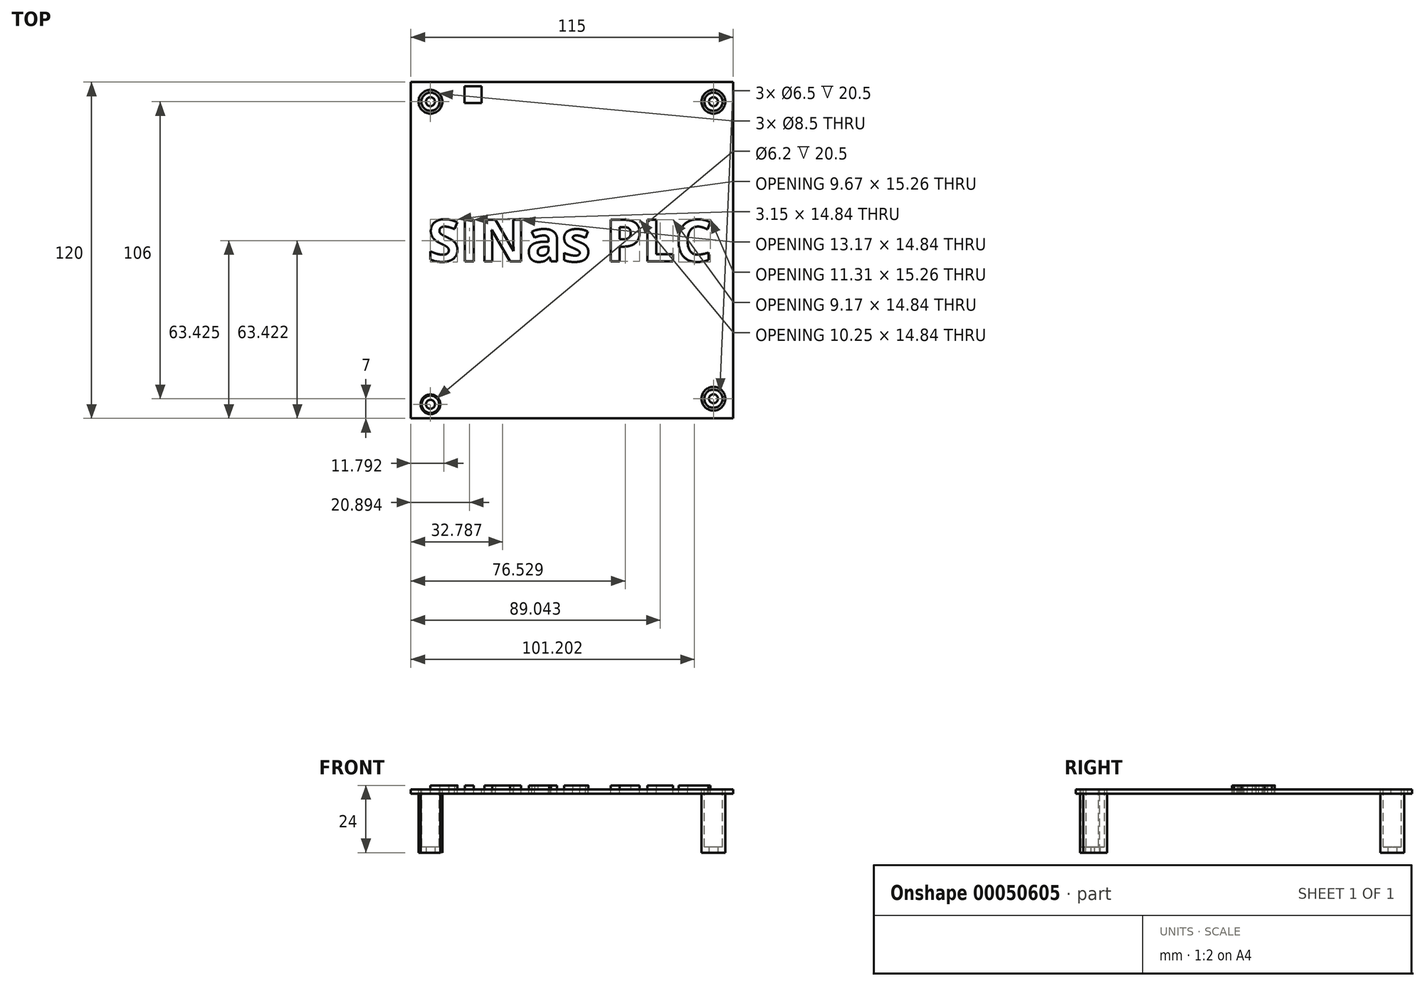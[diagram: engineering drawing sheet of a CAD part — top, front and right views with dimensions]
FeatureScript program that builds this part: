
annotation { "Feature Type Name" : "Feature", "Feature Type Description" : "" }
export const myFeature = defineFeature(function(context is Context, id is Id, definition is map)
    precondition{}
    {
        {
            var Q0;
            Q0=qCreatedBy(makeId("Top.planeOp"),FACE);
            var sketch = newSketch(context, id + "F0", { "sketchPlane" : qUnion([Q0])});
            skLineSegment(sketch, "E0.bottom", {"start": v(-52.5, 65) * mm, "end": v(62.5, 65) * mm});
            skLineSegment(sketch, "E0.top", {"start": v(-52.5, -55) * mm, "end": v(62.5, -55) * mm});
            skLineSegment(sketch, "E0.left", {"start": v(-52.5, 65) * mm, "end": v(-52.5, -55) * mm});
            skLineSegment(sketch, "E0.right", {"start": v(62.5, 65) * mm, "end": v(62.5, -55) * mm});
            skLineSegment(sketch, "E1.rect.bottom", {"start": v(-27.3, 57.5) * mm, "end": v(-33.3, 57.5) * mm});
            skLineSegment(sketch, "E1.rect.top", {"start": v(-27.3, 63.5) * mm, "end": v(-33.3, 63.5) * mm});
            skLineSegment(sketch, "E1.rect.left", {"start": v(-27.3, 57.5) * mm, "end": v(-27.3, 63.5) * mm});
            skLineSegment(sketch, "E1.rect.right", {"start": v(-33.3, 57.5) * mm, "end": v(-33.3, 63.5) * mm});
            skPoint(sketch, "E1.rect.middle", {"position": v(-30.3, 60.5) * mm});
            skCircle(sketch, "E2", {"center": v(-45.5, 58) * mm, "radius": 4.25 * mm});
            skCircle(sketch, "E3", {"center": v(55.5, 58) * mm, "radius": 4.25 * mm});
            skCircle(sketch, "E4", {"center": v(55.5, -48) * mm, "radius": 4.25 * mm});
            skCircle(sketch, "E5", {"center": v(-45.5, -50) * mm, "radius": 3.5 * mm});
            skText(sketch, "E6", { "text": "SINas PLC", "fontName": "OpenSans-Bold.ttf"});
            const initialGuessF0  = {"E6": [-0.0465, 0.001, 1, 0, 0.01497]};
            skSetInitialGuess(sketch, initialGuessF0);
            skSolve(sketch);
        }
        {
            var Q0;
            Q0=makeQuery(id+"F0.imprint","IMPRINT",FACE,{"disambiguationData":[TD([[makeQuery(id+"F0.imprint","IMPRINT",EDGE,{"derivedFrom":sQuery(id+"F0.wireOp",EDGE,"E0.bottom")}),-1.0]])]});
            extrude(context, id + "F1", {"entities" : qUnion([Q0]), "oppositeDirection" : true, "depth" : 1.5 * mm});
        }
        {
            var Q0;
            Q0=makeQuery(id+"F0.imprint","IMPRINT",FACE,{"disambiguationData":[TD([[makeQuery(id+"F0.imprint","IMPRINT",EDGE,{"derivedFrom":sQuery(id+"F0.wireOp",EDGE,"E2")}),1.0]])]});
            var Q1;
            Q1=makeQuery(id+"F0.imprint","IMPRINT",FACE,{"disambiguationData":[TD([[makeQuery(id+"F0.imprint","IMPRINT",EDGE,{"derivedFrom":sQuery(id+"F0.wireOp",EDGE,"E3")}),1.0]])]});
            var Q2;
            Q2=makeQuery(id+"F0.imprint","IMPRINT",FACE,{"disambiguationData":[TD([[makeQuery(id+"F0.imprint","IMPRINT",EDGE,{"derivedFrom":sQuery(id+"F0.wireOp",EDGE,"E5")}),1.0]])]});
            var Q3;
            Q3=makeQuery(id+"F0.imprint","IMPRINT",FACE,{"disambiguationData":[TD([[makeQuery(id+"F0.imprint","IMPRINT",EDGE,{"derivedFrom":sQuery(id+"F0.wireOp",EDGE,"E4")}),1.0]])]});
            extrude(context, id + "F2", {"entities" : qUnion([Q0, Q1, Q2, Q3]), "oppositeDirection" : true, "depth" : 22.5 * mm});
        }
        {
            var Q0;
            Q0=makeQuery(id+"F2.opExtrude","CAP_FACE",FACE,{"disambiguationData":[OSD([sQuery(id+"F0.wireOp",EDGE,"E3")])],"isStart":true});
            var sketch = newSketch(context, id + "F3", { "sketchPlane" : qUnion([Q0])});
            skCircle(sketch, "E7", {"center": v(55.5, 58) * mm, "radius": 3.25 * mm});
            skSolve(sketch);
        }
        {
            var Q0;
            Q0=makeQuery(id+"F3.imprint","IMPRINT",FACE,{"disambiguationData":[TD([[makeQuery(id+"F3.imprint","IMPRINT",EDGE,{"derivedFrom":sQuery(id+"F3.wireOp",EDGE,"E7")}),1.0]])]});
            extrude(context, id + "F4", {"entities" : qUnion([Q0]), "operationType" : NewBodyOperationType.REMOVE, "oppositeDirection" : true, "depth" : 20.5 * mm});
        }
        {
            var Q0;
            Q0=makeQuery(id+"F2.opExtrude","CAP_FACE",FACE,{"disambiguationData":[OSD([sQuery(id+"F0.wireOp",EDGE,"E2")])],"isStart":true});
            var sketch = newSketch(context, id + "F5", { "sketchPlane" : qUnion([Q0])});
            skCircle(sketch, "E8", {"center": v(-45.5, 58) * mm, "radius": 3.25 * mm});
            skSolve(sketch);
        }
        {
            var Q0;
            Q0=makeQuery(id+"F5.imprint","IMPRINT",FACE,{"disambiguationData":[TD([[makeQuery(id+"F5.imprint","IMPRINT",EDGE,{"derivedFrom":sQuery(id+"F5.wireOp",EDGE,"E8")}),1.0]])]});
            extrude(context, id + "F6", {"entities" : qUnion([Q0]), "operationType" : NewBodyOperationType.REMOVE, "oppositeDirection" : true, "depth" : 20.5 * mm});
        }
        {
            var Q0;
            Q0=makeQuery(id+"F2.opExtrude","CAP_FACE",FACE,{"disambiguationData":[OSD([sQuery(id+"F0.wireOp",EDGE,"E5")])],"isStart":true});
            var sketch = newSketch(context, id + "F7", { "sketchPlane" : qUnion([Q0])});
            skCircle(sketch, "E9", {"center": v(-45.5, -50) * mm, "radius": 3.1 * mm});
            skSolve(sketch);
        }
        {
            var Q0;
            Q0=makeQuery(id+"F7.imprint","IMPRINT",FACE,{"disambiguationData":[TD([[makeQuery(id+"F7.imprint","IMPRINT",EDGE,{"derivedFrom":sQuery(id+"F7.wireOp",EDGE,"E9")}),1.0]])]});
            extrude(context, id + "F8", {"entities" : qUnion([Q0]), "operationType" : NewBodyOperationType.REMOVE, "oppositeDirection" : true, "depth" : 20.5 * mm});
        }
        {
            var Q0;
            Q0=makeQuery(id+"F2.opExtrude","CAP_FACE",FACE,{"disambiguationData":[OSD([sQuery(id+"F0.wireOp",EDGE,"E4")])],"isStart":true});
            var sketch = newSketch(context, id + "F9", { "sketchPlane" : qUnion([Q0])});
            skCircle(sketch, "E10", {"center": v(55.5, -48) * mm, "radius": 3.25 * mm});
            skSolve(sketch);
        }
        {
            var Q0;
            Q0=makeQuery(id+"F9.imprint","IMPRINT",FACE,{"disambiguationData":[TD([[makeQuery(id+"F9.imprint","IMPRINT",EDGE,{"derivedFrom":sQuery(id+"F9.wireOp",EDGE,"E10")}),1.0]])]});
            extrude(context, id + "F10", {"entities" : qUnion([Q0]), "operationType" : NewBodyOperationType.REMOVE, "oppositeDirection" : true, "depth" : 20.5 * mm});
        }
        {
            var Q0;
            Q0=makeQuery(id+"F2.opExtrude","CAP_FACE",FACE,{"disambiguationData":[OSD([sQuery(id+"F0.wireOp",EDGE,"E5")])],"isStart":false});
            var sketch = newSketch(context, id + "F11", { "sketchPlane" : qUnion([Q0])});
            skCircle(sketch, "E11", {"center": v(-45.5, 50) * mm, "radius": 1.6 * mm});
            skSolve(sketch);
        }
        {
            var Q0;
            Q0=makeQuery(id+"F11.imprint","IMPRINT",FACE,{"disambiguationData":[TD([[makeQuery(id+"F11.imprint","IMPRINT",EDGE,{"derivedFrom":sQuery(id+"F11.wireOp",EDGE,"E11")}),1.0]])]});
            extrude(context, id + "F12", {"entities" : qUnion([Q0]), "operationType" : NewBodyOperationType.REMOVE, "oppositeDirection" : true, "depth" : 2.5 * mm});
        }
        {
            var Q0;
            Q0=makeQuery(id+"F2.opExtrude","CAP_FACE",FACE,{"disambiguationData":[OSD([sQuery(id+"F0.wireOp",EDGE,"E2")])],"isStart":false});
            var sketch = newSketch(context, id + "F13", { "sketchPlane" : qUnion([Q0])});
            skCircle(sketch, "E12", {"center": v(-45.5, -58) * mm, "radius": 1.6 * mm});
            skSolve(sketch);
        }
        {
            var Q0;
            Q0=makeQuery(id+"F13.imprint","IMPRINT",FACE,{"disambiguationData":[TD([[makeQuery(id+"F13.imprint","IMPRINT",EDGE,{"derivedFrom":sQuery(id+"F13.wireOp",EDGE,"E12")}),1.0]])]});
            extrude(context, id + "F14", {"entities" : qUnion([Q0]), "operationType" : NewBodyOperationType.REMOVE, "oppositeDirection" : true, "depth" : 2.5 * mm});
        }
        {
            var Q0;
            Q0=makeQuery(id+"F2.opExtrude","CAP_FACE",FACE,{"disambiguationData":[OSD([sQuery(id+"F0.wireOp",EDGE,"E3")])],"isStart":false});
            var sketch = newSketch(context, id + "F15", { "sketchPlane" : qUnion([Q0])});
            skCircle(sketch, "E13", {"center": v(55.5, -58) * mm, "radius": 1.6 * mm});
            skSolve(sketch);
        }
        {
            var Q0;
            Q0=makeQuery(id+"F15.imprint","IMPRINT",FACE,{"disambiguationData":[TD([[makeQuery(id+"F15.imprint","IMPRINT",EDGE,{"derivedFrom":sQuery(id+"F15.wireOp",EDGE,"E13")}),1.0]])]});
            extrude(context, id + "F16", {"entities" : qUnion([Q0]), "operationType" : NewBodyOperationType.REMOVE, "oppositeDirection" : true, "depth" : 2.5 * mm});
        }
        {
            var Q0;
            Q0=makeQuery(id+"F2.opExtrude","CAP_FACE",FACE,{"disambiguationData":[OSD([sQuery(id+"F0.wireOp",EDGE,"E4")])],"isStart":false});
            var sketch = newSketch(context, id + "F17", { "sketchPlane" : qUnion([Q0])});
            skCircle(sketch, "E14", {"center": v(55.5, 48) * mm, "radius": 1.6 * mm});
            skSolve(sketch);
        }
        {
            var Q0;
            Q0=makeQuery(id+"F17.imprint","IMPRINT",FACE,{"disambiguationData":[TD([[makeQuery(id+"F17.imprint","IMPRINT",EDGE,{"derivedFrom":sQuery(id+"F17.wireOp",EDGE,"E14")}),1.0]])]});
            extrude(context, id + "F18", {"entities" : qUnion([Q0]), "operationType" : NewBodyOperationType.REMOVE, "oppositeDirection" : true, "depth" : 2.5 * mm});
        }
        {
            var Q0;
            Q0=makeQuery(id+"F0.imprint","IMPRINT",FACE,{"disambiguationData":[TD([[makeQuery(id+"F0.imprint","IMPRINT",EDGE,{"derivedFrom":sQuery(id+"F0.wireOp",EDGE,"E6.sketch_text.stroke-0")}),-1.0]])]});
            extrude(context, id + "F19", {"entities" : qUnion([Q0]), "depth" : 1.5 * mm});
        }
        {
            var Q0;
            Q0=makeQuery(id+"F0.imprint","IMPRINT",FACE,{"disambiguationData":[TD([[makeQuery(id+"F0.imprint","IMPRINT",EDGE,{"derivedFrom":sQuery(id+"F0.wireOp",EDGE,"E6.sketch_text.stroke-28")}),-1.0]])]});
            var Q1;
            Q1=makeQuery(id+"F0.imprint","IMPRINT",FACE,{"disambiguationData":[TD([[makeQuery(id+"F0.imprint","IMPRINT",EDGE,{"derivedFrom":sQuery(id+"F0.wireOp",EDGE,"E6.sketch_text.stroke-32")}),-1.0]])]});
            var Q2;
            Q2=makeQuery(id+"F0.imprint","IMPRINT",FACE,{"disambiguationData":[TD([[makeQuery(id+"F0.imprint","IMPRINT",EDGE,{"derivedFrom":sQuery(id+"F0.wireOp",EDGE,"E6.sketch_text.stroke-46")}),-1.0]])]});
            var Q3;
            Q3=makeQuery(id+"F0.imprint","IMPRINT",FACE,{"disambiguationData":[TD([[makeQuery(id+"F0.imprint","IMPRINT",EDGE,{"derivedFrom":sQuery(id+"F0.wireOp",EDGE,"E6.sketch_text.stroke-71")}),-1.0]])]});
            var Q4;
            Q4=makeQuery(id+"F0.imprint","IMPRINT",FACE,{"disambiguationData":[TD([[makeQuery(id+"F0.imprint","IMPRINT",EDGE,{"derivedFrom":sQuery(id+"F0.wireOp",EDGE,"E6.sketch_text.stroke-97")}),-1.0]])]});
            var Q5;
            Q5=makeQuery(id+"F0.imprint","IMPRINT",FACE,{"disambiguationData":[TD([[makeQuery(id+"F0.imprint","IMPRINT",EDGE,{"derivedFrom":sQuery(id+"F0.wireOp",EDGE,"E6.sketch_text.stroke-113")}),-1.0]])]});
            var Q6;
            Q6=makeQuery(id+"F0.imprint","IMPRINT",FACE,{"disambiguationData":[TD([[makeQuery(id+"F0.imprint","IMPRINT",EDGE,{"derivedFrom":sQuery(id+"F0.wireOp",EDGE,"E6.sketch_text.stroke-119")}),-1.0]])]});
            extrude(context, id + "F20", {"entities" : qUnion([Q0, Q1, Q2, Q3, Q4, Q5, Q6]), "depth" : 1.5 * mm});
        }
    });
